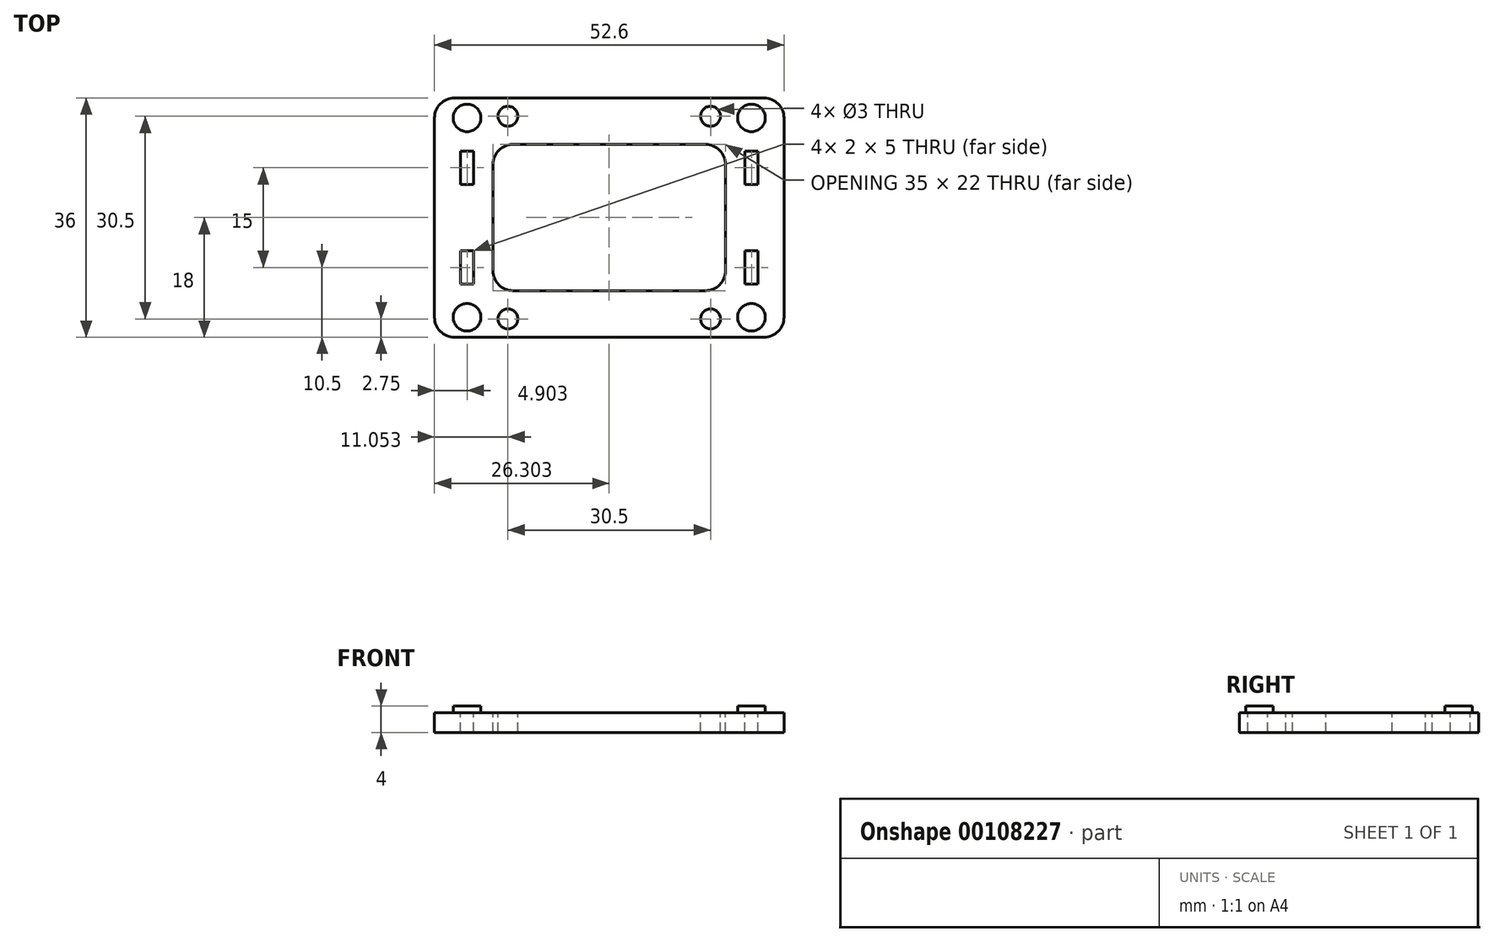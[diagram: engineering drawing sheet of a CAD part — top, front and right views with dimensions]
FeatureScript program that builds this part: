
annotation { "Feature Type Name" : "Feature", "Feature Type Description" : "" }
export const myFeature = defineFeature(function(context is Context, id is Id, definition is map)
    precondition{}
    {
        {
            var Q0;
            Q0=qCreatedBy(makeId("Top.planeOp"),FACE);
            var sketch = newSketch(context, id + "F0", { "sketchPlane" : qUnion([Q0])});
            skLineSegment(sketch, "E0.bottom", {"start": v(-30.65, 22.16) * mm, "end": v(21.95, 22.16) * mm});
            skLineSegment(sketch, "E0.top", {"start": v(-30.65, -13.84) * mm, "end": v(21.95, -13.84) * mm});
            skLineSegment(sketch, "E0.left", {"start": v(-30.65, 22.16) * mm, "end": v(-30.65, -13.84) * mm});
            skLineSegment(sketch, "E0.right", {"start": v(21.95, 22.16) * mm, "end": v(21.95, -13.84) * mm});
            skSolve(sketch);
        }
        {
            var Q0;
            Q0=qSketchRegion(id+"F0",true);
            extrude(context, id + "F1", {"entities" : qUnion([Q0]), "depth" : 3 * mm});
        }
        {
            var Q0;
            Q0=makeQuery(id+"F1.opExtrude","CAP_FACE",FACE,{"disambiguationData":[OSD([sQuery(id+"F0.wireOp",EDGE,"E0.bottom"),sQuery(id+"F0.wireOp",EDGE,"E0.top"),sQuery(id+"F0.wireOp",EDGE,"E0.left"),sQuery(id+"F0.wireOp",EDGE,"E0.right")])],"isStart":false});
            var sketch = newSketch(context, id + "F2", { "sketchPlane" : qUnion([Q0])});
            skCircle(sketch, "E1", {"center": v(-25.75, 19.16) * mm, "radius": 2.08 * mm});
            skCircle(sketch, "E2", {"center": v(17.05, 19.16) * mm, "radius": 2.08 * mm});
            skCircle(sketch, "E3", {"center": v(17.05, -10.84) * mm, "radius": 2.08 * mm});
            skCircle(sketch, "E4", {"center": v(-25.75, -10.84) * mm, "radius": 2.08 * mm});
            skSolve(sketch);
        }
        {
            var Q0;
            Q0=qSketchRegion(id+"F2",true);
            extrude(context, id + "F3", {"entities" : qUnion([Q0]), "operationType" : NewBodyOperationType.ADD, "depth" : 1 * mm});
        }
        {
            var Q0;
            Q0=makeQuery(id+"F1.opExtrude","CAP_FACE",FACE,{"disambiguationData":[OSD([sQuery(id+"F0.wireOp",EDGE,"E0.bottom"),sQuery(id+"F0.wireOp",EDGE,"E0.top"),sQuery(id+"F0.wireOp",EDGE,"E0.left"),sQuery(id+"F0.wireOp",EDGE,"E0.right")])],"isStart":false});
            var sketch = newSketch(context, id + "F4", { "sketchPlane" : qUnion([Q0])});
            skLineSegment(sketch, "E5", {"start": v(-25.75, 19.16) * mm, "end": v(-25.75, -10.84) * mm, "construction": true});
            skLineSegment(sketch, "E6", {"start": v(-25.75, -10.84) * mm, "end": v(17.05, -10.84) * mm, "construction": true});
            skLineSegment(sketch, "E7", {"start": v(17.05, -10.84) * mm, "end": v(17.05, 19.16) * mm, "construction": true});
            skLineSegment(sketch, "E8", {"start": v(17.05, 19.16) * mm, "end": v(-25.75, 19.16) * mm, "construction": true});
            skLineSegment(sketch, "E9.bottom", {"start": v(-26.75, 14.16) * mm, "end": v(-24.75, 14.16) * mm});
            skLineSegment(sketch, "E9.top", {"start": v(-26.75, 9.16) * mm, "end": v(-24.75, 9.16) * mm});
            skLineSegment(sketch, "E9.left", {"start": v(-26.75, 14.16) * mm, "end": v(-26.75, 9.16) * mm});
            skLineSegment(sketch, "E9.right", {"start": v(-24.75, 14.16) * mm, "end": v(-24.75, 9.16) * mm});
            skLineSegment(sketch, "E10", {"start": v(-25.75, 4.16) * mm, "end": v(17.05, 4.16) * mm, "construction": true});
            skLineSegment(sketch, "E11", {"start": v(-4.35, 19.16) * mm, "end": v(-4.35, -10.84) * mm, "construction": true});
            skLineSegment(sketch, "E12.0.MirrorCS", {"start": v(18.05, 9.16) * mm, "end": v(16.05, 9.16) * mm});
            skLineSegment(sketch, "E12.1.MirrorCS", {"start": v(18.05, 14.16) * mm, "end": v(16.05, 14.16) * mm});
            skLineSegment(sketch, "E12.2.MirrorCS", {"start": v(18.05, 14.16) * mm, "end": v(18.05, 9.16) * mm});
            skLineSegment(sketch, "E12.3.MirrorCS", {"start": v(16.05, 14.16) * mm, "end": v(16.05, 9.16) * mm});
            skLineSegment(sketch, "E13.0.MirrorCS", {"start": v(16.05, -5.84) * mm, "end": v(16.05, -0.84) * mm});
            skLineSegment(sketch, "E13.1.MirrorCS", {"start": v(18.05, -0.84) * mm, "end": v(16.05, -0.84) * mm});
            skLineSegment(sketch, "E13.2.MirrorCS", {"start": v(18.05, -5.84) * mm, "end": v(16.05, -5.84) * mm});
            skLineSegment(sketch, "E13.3.MirrorCS", {"start": v(18.05, -5.84) * mm, "end": v(18.05, -0.84) * mm});
            skLineSegment(sketch, "E13.4.MirrorCS", {"start": v(-26.75, -5.84) * mm, "end": v(-24.75, -5.84) * mm});
            skLineSegment(sketch, "E13.5.MirrorCS", {"start": v(-24.75, -5.84) * mm, "end": v(-24.75, -0.84) * mm});
            skLineSegment(sketch, "E13.6.MirrorCS", {"start": v(-26.75, -5.84) * mm, "end": v(-26.75, -0.84) * mm});
            skLineSegment(sketch, "E13.7.MirrorCS", {"start": v(-26.75, -0.84) * mm, "end": v(-24.75, -0.84) * mm});
            skSolve(sketch);
        }
        {
            var Q0;
            Q0=qSketchRegion(id+"F4",true);
            extrude(context, id + "F5", {"entities" : qUnion([Q0]), "operationType" : NewBodyOperationType.REMOVE, "oppositeDirection" : true, "depth" : 25 * mm});
        }
        {
            var Q0;
            Q0=makeQuery(id+"F1.opExtrude","CAP_FACE",FACE,{"disambiguationData":[OSD([sQuery(id+"F0.wireOp",EDGE,"E0.bottom"),sQuery(id+"F0.wireOp",EDGE,"E0.top"),sQuery(id+"F0.wireOp",EDGE,"E0.left"),sQuery(id+"F0.wireOp",EDGE,"E0.right")])],"isStart":false});
            var sketch = newSketch(context, id + "F6", { "sketchPlane" : qUnion([Q0])});
            skCircle(sketch, "E14", {"center": v(-19.6, 19.41) * mm, "radius": 1.5 * mm});
            skCircle(sketch, "E15", {"center": v(10.9, 19.41) * mm, "radius": 1.5 * mm});
            skCircle(sketch, "E16", {"center": v(-19.6, -11.09) * mm, "radius": 1.5 * mm});
            skCircle(sketch, "E17", {"center": v(10.9, -11.09) * mm, "radius": 1.5 * mm});
            skLineSegment(sketch, "E18.bottom", {"start": v(-18.85, 15.16) * mm, "end": v(10.15, 15.16) * mm});
            skLineSegment(sketch, "E18.top", {"start": v(-18.85, -6.84) * mm, "end": v(10.15, -6.84) * mm});
            skLineSegment(sketch, "E18.left", {"start": v(-21.85, 12.16) * mm, "end": v(-21.85, -3.84) * mm});
            skLineSegment(sketch, "E18.right", {"start": v(13.15, 12.16) * mm, "end": v(13.15, -3.84) * mm});
            skPoint(sketch, "E19.visualSharp", {"position": v(-21.85, 15.16) * mm});
            skArc(sketch, "E19.filletArc", {"start": v(-18.85, 15.16) * mm, "mid": v(-20.97, 14.28) * mm, "end": v(-21.85, 12.16) * mm});
            skPoint(sketch, "E20.visualSharp", {"position": v(-21.85, -6.84) * mm});
            skArc(sketch, "E20.filletArc", {"start": v(-21.85, -3.84) * mm, "mid": v(-20.97, -5.96) * mm, "end": v(-18.85, -6.84) * mm});
            skPoint(sketch, "E21.visualSharp", {"position": v(13.15, -6.84) * mm});
            skArc(sketch, "E21.filletArc", {"start": v(10.15, -6.84) * mm, "mid": v(12.27, -5.96) * mm, "end": v(13.15, -3.84) * mm});
            skPoint(sketch, "E22.visualSharp", {"position": v(13.15, 15.16) * mm});
            skArc(sketch, "E22.filletArc", {"start": v(13.15, 12.16) * mm, "mid": v(12.27, 14.28) * mm, "end": v(10.15, 15.16) * mm});
            skSolve(sketch);
        }
        {
            var Q0;
            Q0=qSketchRegion(id+"F6",true);
            extrude(context, id + "F7", {"entities" : qUnion([Q0]), "operationType" : NewBodyOperationType.REMOVE, "oppositeDirection" : true, "depth" : 25 * mm});
        }
        {
            var Q0;
            Q0=makeQuery(id+"F1.opExtrude","SWEPT_EDGE",EDGE,{"disambiguationData":[OSD([sQuery(id+"F0.wireOp",EDGE,"E0.top"),sQuery(id+"F0.wireOp",EDGE,"E0.left")])]});
            var Q1;
            Q1=makeQuery(id+"F1.opExtrude","SWEPT_EDGE",EDGE,{"disambiguationData":[OSD([sQuery(id+"F0.wireOp",EDGE,"E0.top"),sQuery(id+"F0.wireOp",EDGE,"E0.right")])]});
            var Q2;
            Q2=makeQuery(id+"F1.opExtrude","SWEPT_EDGE",EDGE,{"disambiguationData":[OSD([sQuery(id+"F0.wireOp",EDGE,"E0.bottom"),sQuery(id+"F0.wireOp",EDGE,"E0.right")])]});
            var Q3;
            Q3=makeQuery(id+"F1.opExtrude","SWEPT_EDGE",EDGE,{"disambiguationData":[OSD([sQuery(id+"F0.wireOp",EDGE,"E0.bottom"),sQuery(id+"F0.wireOp",EDGE,"E0.left")])]});
            fillet(context, id + "F8", {"entities" : qUnion([Q0, Q1, Q2, Q3]), "radius" : 3 * mm, "tangentPropagation" : true, "allowEdgeOverflow" : false});
        }
    });
